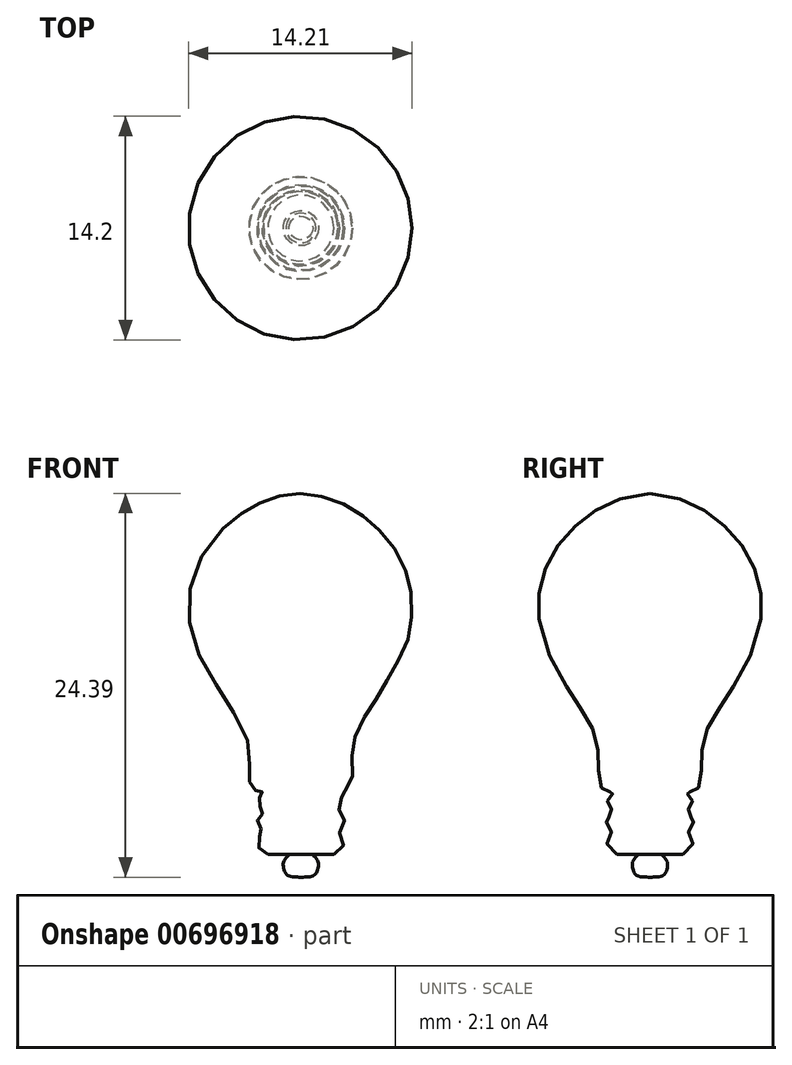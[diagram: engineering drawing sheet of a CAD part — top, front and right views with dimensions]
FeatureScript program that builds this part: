
annotation { "Feature Type Name" : "Feature", "Feature Type Description" : "" }
export const myFeature = defineFeature(function(context is Context, id is Id, definition is map)
    precondition{}
    {
        {
            var Q0;
            Q0=qCreatedBy(makeId("Front.planeOp"),FACE);
            var sketch = newSketch(context, id + "F0", { "sketchPlane" : qUnion([Q0])});
            skFitSpline(sketch, "E0", {"points": [v(-12.37, 24.8) * mm, v(-11.17, 24.65) * mm, v(-9.84, 24.21) * mm, v(-8.63, 23.55) * mm, v(-7.69, 22.78) * mm, v(-6.8, 21.86) * mm, v(-5.9, 20.42) * mm, v(-5.46, 19.2) * mm, v(-5.26, 17.84) * mm, v(-5.38, 16.17) * mm, v(-5.67, 15.07) * mm, v(-6.4, 13.74) * mm, v(-7.02, 12.62) * mm, v(-7.66, 11.54) * mm, v(-8.3, 10.57) * mm, v(-8.87, 9.42) * mm, v(-9.04, 8.55) * mm, v(-9.07, 7.32) * mm, v(-9.07, 6.5) * mm, v(-9.5, 5.91) * mm, v(-10, 5.78) * mm, v(-9.68, 5.4) * mm, v(-9.74, 4.93) * mm, v(-9.94, 4.58) * mm, v(-9.72, 4.25) * mm, v(-9.56, 3.87) * mm, v(-9.88, 3.36) * mm, v(-9.7, 2.99) * mm, v(-9.6, 2.54) * mm, v(-9.76, 2.1) * mm, v(-10.23, 1.87) * mm], "startDerivative": vector(30.97, -2.64) * mm, "endDerivative": vector(-21.33, -6.95) * mm});
            skFitSpline(sketch, "E1", {"points": [v(-10.23, 1.87) * mm, v(-11.37, 1.87) * mm, v(-11.57, 1.87) * mm, v(-11.27, 1.5) * mm, v(-11.21, 1.06) * mm, v(-11.4, 0.6) * mm, v(-11.84, 0.43) * mm, v(-12.57, 0.41) * mm], "startDerivative": vector(-6.24, -0.2) * mm, "endDerivative": vector(-4.56, 0.03) * mm});
            skLineSegment(sketch, "E2", {"start": v(-12.37, 24.8) * mm, "end": v(-12.31, -1.9) * mm});
            skLineSegment(sketch, "E3", {"start": v(-11.37, 1.87) * mm, "end": v(-10.23, 1.87) * mm});
            skLineSegment(sketch, "E4", {"start": v(-11.98, 24.77) * mm, "end": v(-12.37, 24.8) * mm});
            skSolve(sketch);
        }
        {
            var Q0;
            {var subQ0=sQuery(id+"F0.wireOp",EDGE,"E0");Q0=makeQuery(id+"F0.imprint","IMPRINT",FACE,{"disambiguationData":[TD([[makeQuery(id+"F0.imprint","IMPRINT",EDGE,{"derivedFrom":subQ0}),-1.0]])]});}
            var Q1;
            Q1=sQuery(id+"F0.wireOp",EDGE,"E2");
            revolve(context, id + "F1", {"entities" : qUnion([Q0]), "axis" : qUnion([Q1]), "revolveType" : RevolveType.FULL});
        }
    });
